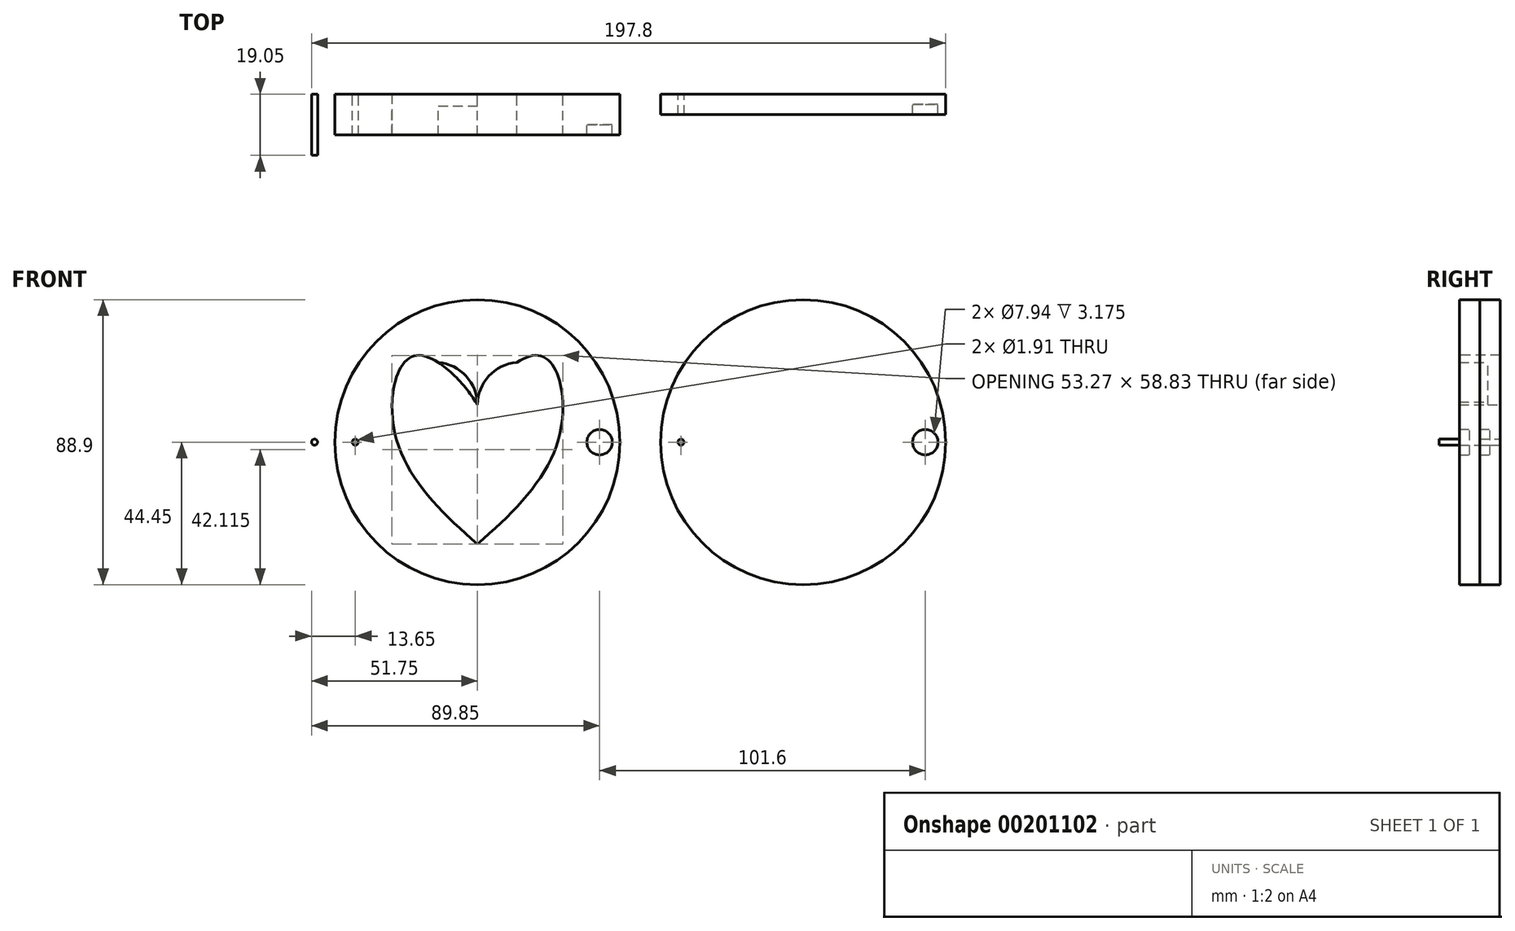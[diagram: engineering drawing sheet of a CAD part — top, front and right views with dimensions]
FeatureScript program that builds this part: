
annotation { "Feature Type Name" : "Feature", "Feature Type Description" : "" }
export const myFeature = defineFeature(function(context is Context, id is Id, definition is map)
    precondition{}
    {
        {
            var Q0;
            Q0=qCreatedBy(makeId("Front.planeOp"),FACE);
            var sketch = newSketch(context, id + "F0", { "sketchPlane" : qUnion([Q0])});
            skCircle(sketch, "E0", {"center": v(0, 0) * mm, "radius": 44.45 * mm});
            skCircle(sketch, "E1.0", {"center": v(0, 0) * mm, "radius": 31.75 * mm, "construction": true});
            skCircle(sketch, "E2", {"center": v(101.6, 0) * mm, "radius": 44.45 * mm});
            skCircle(sketch, "E3", {"center": v(38.1, 0) * mm, "radius": 3.97 * mm});
            skLineSegment(sketch, "E4", {"start": v(31.75, 0) * mm, "end": v(44.45, 0) * mm, "construction": true});
            skCircle(sketch, "E5", {"center": v(139.7, 0) * mm, "radius": 3.97 * mm});
            skLineSegment(sketch, "E6", {"start": v(146.05, 0) * mm, "end": v(133.35, 0) * mm, "construction": true});
            skCircle(sketch, "E7", {"center": v(-38.1, 0) * mm, "radius": 0.95 * mm});
            skLineSegment(sketch, "E8", {"start": v(-31.75, 0) * mm, "end": v(-44.45, 0) * mm, "construction": true});
            skLineSegment(sketch, "E9", {"start": v(57.15, 0) * mm, "end": v(69.85, 0) * mm, "construction": true});
            skCircle(sketch, "E10", {"center": v(63.5, 0) * mm, "radius": 0.95 * mm});
            skCircle(sketch, "E11", {"center": v(-50.8, 0) * mm, "radius": 0.95 * mm});
            skArc(sketch, "E12", {"start": v(0, 11.59) * mm, "mid": v(-13.32, 24.9) * mm, "end": v(-26.64, 11.59) * mm});
            skArc(sketch, "E13", {"start": v(26.64, 11.59) * mm, "mid": v(13.32, 24.9) * mm, "end": v(0, 11.59) * mm});
            skLineSegment(sketch, "E14", {"start": v(-26.64, 11.59) * mm, "end": v(26.64, 11.59) * mm, "construction": true});
            skLineSegment(sketch, "E15", {"start": v(26.64, 11.59) * mm, "end": v(0, -31.75) * mm, "construction": true});
            skPoint(sketch, "E15.endSnap0", {"position": v(0, 11.59) * mm});
            skLineSegment(sketch, "E16", {"start": v(0, -31.75) * mm, "end": v(-26.64, 11.59) * mm, "construction": true});
            skFitSpline(sketch, "E17.trimOffspring", {"points": [v(0, 11.59) * mm, v(-19.15, 27.04) * mm, v(-26.03, 4.06) * mm, v(0, -31.75) * mm], "startDerivative": vector(-32.4, 61.17) * mm, "endDerivative": vector(91.17, -77.96) * mm});
            skLineSegment(sketch, "E18", {"start": v(0, 11.59) * mm, "end": v(0, -31.75) * mm, "construction": true});
            skFitSpline(sketch, "E19.MirrorCS", {"points": [v(0, 11.59) * mm, v(19.15, 27.04) * mm, v(26.03, 4.06) * mm, v(0, -31.75) * mm], "startDerivative": vector(32.4, 61.17) * mm, "endDerivative": vector(-91.17, -77.96) * mm});
            skPoint(sketch, "E20", {"position": v(0, -10.08) * mm});
            skSolve(sketch);
        }
        {
            var Q0;
            Q0=makeQuery(id+"F0.imprint","IMPRINT",FACE,{"disambiguationData":[TD([[makeQuery(id+"F0.imprint","IMPRINT",EDGE,{"derivedFrom":sQuery(id+"F0.wireOp",EDGE,"E0")}),1.0]])]});
            extrude(context, id + "F1", {"entities" : qUnion([Q0]), "depth" : 12.7 * mm});
        }
        {
            var Q0;
            Q0=makeQuery(id+"F0.imprint","IMPRINT",FACE,{"disambiguationData":[TD([[makeQuery(id+"F0.imprint","IMPRINT",EDGE,{"derivedFrom":sQuery(id+"F0.wireOp",EDGE,"E12")}),1.0]])]});
            extrude(context, id + "F2", {"entities" : qUnion([Q0]), "operationType" : NewBodyOperationType.ADD, "depth" : 3.8 * mm});
        }
        {
            var Q0;
            Q0=makeQuery(id+"F0.imprint","IMPRINT",FACE,{"disambiguationData":[TD([[makeQuery(id+"F0.imprint","IMPRINT",EDGE,{"derivedFrom":sQuery(id+"F0.wireOp",EDGE,"E3")}),1.0]])]});
            extrude(context, id + "F3", {"entities" : qUnion([Q0]), "operationType" : NewBodyOperationType.ADD, "depth" : 9.52 * mm});
        }
        {
            var Q0;
            Q0=makeQuery(id+"F0.imprint","IMPRINT",FACE,{"disambiguationData":[TD([[makeQuery(id+"F0.imprint","IMPRINT",EDGE,{"derivedFrom":sQuery(id+"F0.wireOp",EDGE,"E2")}),1.0]])]});
            extrude(context, id + "F4", {"entities" : qUnion([Q0]), "depth" : 6.35 * mm});
        }
        {
            var Q0;
            Q0=makeQuery(id+"F0.imprint","IMPRINT",FACE,{"disambiguationData":[TD([[makeQuery(id+"F0.imprint","IMPRINT",EDGE,{"derivedFrom":sQuery(id+"F0.wireOp",EDGE,"E5")}),1.0]])]});
            extrude(context, id + "F5", {"entities" : qUnion([Q0]), "operationType" : NewBodyOperationType.ADD, "depth" : 3.17 * mm});
        }
        {
            var Q0;
            Q0=makeQuery(id+"F0.imprint","IMPRINT",FACE,{"disambiguationData":[TD([[makeQuery(id+"F0.imprint","IMPRINT",EDGE,{"derivedFrom":sQuery(id+"F0.wireOp",EDGE,"E11")}),1.0]])]});
            extrude(context, id + "F6", {"entities" : qUnion([Q0]), "depth" : 19.05 * mm});
        }
    });
